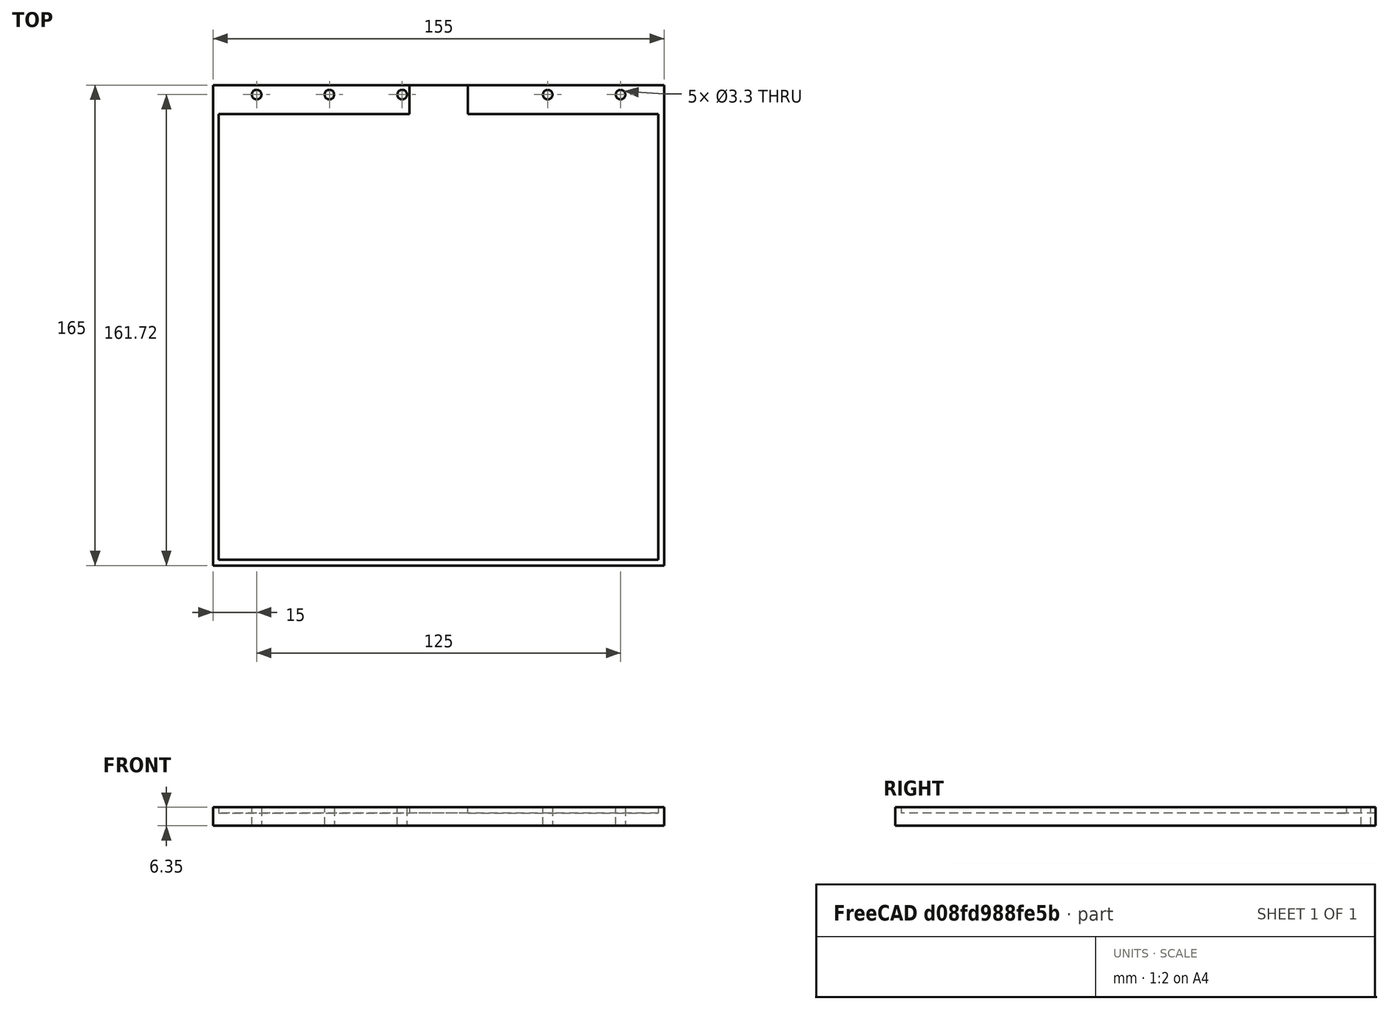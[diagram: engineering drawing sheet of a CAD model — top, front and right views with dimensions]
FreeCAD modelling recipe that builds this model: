
FCSTD DOCUMENT  (FreeCAD 0.19R)
Label: BedBottomMount
License: All rights reserved
LicenseURL: http://en.wikipedia.org/wiki/All_rights_reserved
objects: Sketcher::SketchObject×4, PartDesign::Pocket×3, PartDesign::Pad×1, PartDesign::Body×1, Mesh::Feature×1
note: 13 computed .brp shape members not serialized (recipe doc carries the construction recipe); baked Part::Feature solids carry a one-line shape summary decoded from their .brp

FEATURE [Sketcher::SketchObject] Sketch
  FullyConstrained = true
  MapMode = 5
  Support = -> [XY_Plane]
  sketch-geometry (4):
    g0: LineSegment StartX=-77.5 StartY=85 StartZ=0 EndX=77.5 EndY=85 EndZ=0
    g1: LineSegment StartX=77.5 StartY=85 StartZ=0 EndX=77.5 EndY=-80 EndZ=0
    g2: LineSegment StartX=77.5 StartY=-80 StartZ=0 EndX=-77.5 EndY=-80 EndZ=0
    g3: LineSegment StartX=-77.5 StartY=-80 StartZ=0 EndX=-77.5 EndY=85 EndZ=0
  constraints (11):
    c: Coincident(g0,g1)
    c: Coincident(g1,g2)
    c: Coincident(g2,g3)
    c: Coincident(g3,g0)
    c: Horizontal(g0)
    c: Vertical(g1)
    c: Vertical(g3)
    c: Distance(g0) = 155
    c: Distance(g1) = 165
    c: Symmetric(g1,g2,g-2)
    c: DistanceY(g1) = -80
FEATURE [PartDesign::Pad] Pad
  Direction = (1,1,1)
  Length = 6.35
  Length2 = 100
  Profile = -> Sketch
  Type = 0
FEATURE [Sketcher::SketchObject] Sketch001
  ExternalGeometry = -> [Pad]
  FullyConstrained = true
  MapMode = 5
  Placement = pos=(0,0,6.35) rot=(0,0,1;0rad)
  Support = -> [Pad]
  sketch-geometry (4):
    g0: LineSegment StartX=-75.5 StartY=75 StartZ=0 EndX=75.5 EndY=75 EndZ=0
    g1: LineSegment StartX=75.5 StartY=75 StartZ=0 EndX=75.5 EndY=-78 EndZ=0
    g2: LineSegment StartX=75.5 StartY=-78 StartZ=0 EndX=-75.5 EndY=-78 EndZ=0
    g3: LineSegment StartX=-75.5 StartY=-78 StartZ=0 EndX=-75.5 EndY=75 EndZ=0
  constraints (11):
    c: Coincident(g0,g1)
    c: Coincident(g1,g2)
    c: Coincident(g2,g3)
    c: Coincident(g3,g0)
    c: Horizontal(g2)
    c: Vertical(g1)
    c: Vertical(g3)
    c: Symmetric(g0,g0,g-2)
    c: Distance(g1,g-3) = 2
    c: Distance(g0) = 151
    c: Distance(g1) = 153
FEATURE [PartDesign::Pocket] Pocket
  BaseFeature = -> Pad
  Length = 2
  Length2 = 100
  Profile = -> Sketch001
  Type = 0
FEATURE [Sketcher::SketchObject] Sketch003
  ExternalGeometry = -> [Pocket]
  FullyConstrained = false
  MapMode = 5
  Placement = pos=(0,0,6.35) rot=(0,0,1;0rad)
  Support = -> [Pocket]
  sketch-geometry (10):
    g0: LineSegment StartX=-68.3286 StartY=85 StartZ=0 EndX=56.9479 EndY=85 EndZ=0
    g1: LineSegment StartX=56.9479 StartY=85 StartZ=0 EndX=56.9479 EndY=81.72 EndZ=0
    g2: LineSegment StartX=56.9479 StartY=81.72 StartZ=0 EndX=-68.3286 EndY=81.72 EndZ=0
    g3: LineSegment StartX=-68.3286 StartY=81.72 StartZ=0 EndX=-68.3286 EndY=85 EndZ=0
    g4: Circle CenterX=-37.5 CenterY=81.72 CenterZ=0 NormalX=0 NormalY=0 NormalZ=1 AngleXU=0 Radius=1.65
    g5: Circle CenterX=-12.5 CenterY=81.72 CenterZ=0 NormalX=0 NormalY=0 NormalZ=1 AngleXU=0 Radius=1.65
    g6: Circle CenterX=62.5 CenterY=81.72 CenterZ=0 NormalX=0 NormalY=0 NormalZ=1 AngleXU=0 Radius=1.65
    g7: Circle CenterX=-62.5 CenterY=81.72 CenterZ=0 NormalX=0 NormalY=0 NormalZ=1 AngleXU=0 Radius=1.65
    g8: Circle CenterX=37.5 CenterY=81.72 CenterZ=0 NormalX=0 NormalY=0 NormalZ=1 AngleXU=0 Radius=1.65
    g9: Circle CenterX=12.5 CenterY=81.72 CenterZ=0 NormalX=0 NormalY=0 NormalZ=1 AngleXU=0 Radius=1.65
  constraints (27):
    c: Coincident(g0,g1)
    c: Coincident(g1,g2)
    c: Coincident(g2,g3)
    c: Coincident(g3,g0)
    c: Horizontal(g0)
    c: Horizontal(g2)
    c: Vertical(g1)
    c: Vertical(g3)
    c: Distance(g1) = 3.28
    c: PointOnObject(g0,g-3)
    c: PointOnObject(g6,g2)
    c: PointOnObject(g4,g2)
    c: PointOnObject(g5,g2)
    c: Diameter(g4) = 3.3
    c: Equal(g4,g5)
    c: Equal(g4,g6)
    c: Diameter(g7) = 3.3
    c: Distance(g4,g7) = 25
    c: PointOnObject(g7,g2)
    c: Distance(g5,g4) = 25
    c: PointOnObject(g8,g2)
    c: Diameter(g8) = 3.3
    c: Distance(g8,g6) = 25
    c: Distance(g8,g5) = 50
    c: Diameter(g9) = 3.3
    c: Distance(g9,g5) = 25
    c: Symmetric(g9,g5,g-2)
FEATURE [PartDesign::Pocket] Pocket001
  BaseFeature = -> Pocket
  Length = 5
  Length2 = 100
  Profile = -> Sketch003
  Type = 1
FEATURE [Sketcher::SketchObject] Sketch004
  FullyConstrained = false
  MapMode = 5
  Placement = pos=(0,0,6.35) rot=(0,0,1;0rad)
  Support = -> [Pocket001]
  sketch-geometry (4):
    g0: LineSegment StartX=-10 StartY=93.1749 StartZ=0 EndX=10 EndY=93.1749 EndZ=0
    g1: LineSegment StartX=10 StartY=93.1749 StartZ=0 EndX=10 EndY=71.6902 EndZ=0
    g2: LineSegment StartX=10 StartY=71.6902 StartZ=0 EndX=-10 EndY=71.6902 EndZ=0
    g3: LineSegment StartX=-10 StartY=71.6902 StartZ=0 EndX=-10 EndY=93.1749 EndZ=0
  constraints (9):
    c: Coincident(g0,g1)
    c: Coincident(g1,g2)
    c: Coincident(g2,g3)
    c: Coincident(g3,g0)
    c: Horizontal(g2)
    c: Vertical(g1)
    c: Vertical(g3)
    c: Symmetric(g0,g0,g-2)
    c: Distance(g0) = 20
FEATURE [PartDesign::Pocket] Pocket002
  BaseFeature = -> Pocket001
  Length = 2
  Length2 = 100
  Profile = -> Sketch004
  Type = 0
FEATURE [PartDesign::Body] Body
  Group = -> [Sketch,Pad,Sketch001,Pocket,Sketch003,Pocket001,Sketch004,Pocket002]
  Origin = -> Origin
  Tip = -> Pocket002
FEATURE [Mesh::Feature] Mesh  label="Pocket002 (Meshed)"
